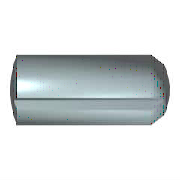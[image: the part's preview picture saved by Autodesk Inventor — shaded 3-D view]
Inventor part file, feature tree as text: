
AUTODESK INVENTOR PART (.ipt)
format: ipt  version: 2021 (Build 250183000, 183)  size: 145,920 bytes
history: native  units: mm (DEFAULTED — no unit token found)
features: sketch x2, extrude x1, pattern_circular x1
ambient origin geometry x8: Origin, YZ Plane, XZ Plane, XY Plane, X Axis, Y Axis, Z Axis, Center Point
bodies: Solid1 (feature_tree), Body (feature_tree)
feature tree (4):
  extrude  "Groove"  Depth=20.0mm
  pattern_circular  "Grooves"  Angle=15.0deg  [1 undecoded]
  sketch  "Sketch1"  dims[d0=100.0mm d1=20.0mm]
  sketch  "Sketch2"  dims[d2=5.2mm d3=15.0deg d4=2.5mm d5=2.5mm d9=90.0deg d6=6.108652mm d7=6.108652mm d8=1.0mm d15=10.0mm d10=0.0mm d11=30.0mm d12=360.0deg d13=-2.5mm d28=2.5mm d29=0.0mm]
note: 1 required parameter value undecoded (feature->parameter linkage not recoverable at this tier; creation-order binding heuristic only, values carry confidence <= 0.55)
